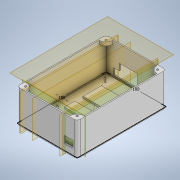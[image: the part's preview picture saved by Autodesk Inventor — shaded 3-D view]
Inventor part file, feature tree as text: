
AUTODESK INVENTOR PART (.ipt)
format: ipt  version: 2021 (Build 250183000, 183)  size: 476,160 bytes
history: native  units: in
note: dims shown in document units (in); Inventor stores cm internally (conversion verified against a paired STEP export)
features: sketch x25, extrude x19, reference x16, plane x7, mirror x4, other x4, revolve x2, chamfer x1, fillet x1
ambient origin geometry x8: Origin, YZ Plane, XZ Plane, XY Plane, X Axis, Y Axis, Z Axis, Center Point
bodies: Solid1 (feature_tree)
feature tree (79):
  sketch  "Sketch1"  dims[d0=3.937in d1=5.9055in]
  extrude  "Extrusion1"  Depth=5.9055in
  extrude  "Extrusion2"  Depth=2.1654in TaperAngle=0.0deg
  sketch  "Sketch2"  dims[d5=0.0787in d6=0.0in d7=-1.5748in]
  plane  "Work Plane1"
  extrude  "Extrusion3"  [1 undecoded]
  sketch  "Sketch7"  dims[d19=0.1181in d20=0.0in d21=2.8346in]
  plane  "Work Plane2"
  revolve  "Revolution2"  [1 undecoded]
  plane  "Work Plane3"
  extrude  "Extrusion4"  Depth=0.7087in
  sketch  "Sketch Driven Pattern1"  dims[d2=0.0787in d3=2.1654in d4=0.0in]
  extrude  "Extrusion5"  Depth=2.8346in
  plane  "Work Plane4"
  extrude  "Extrusion6"  Depth=0.1102in
  extrude  "Extrusion7"  Depth=0.1339in
  extrude  "Extrusion8"  TaperAngle=90.0deg  [1 undecoded]
  mirror  "Mirror1"
  plane  "Work Plane5"
  extrude  "Extrusion9"  Depth=0.0118in
  extrude  "Extrusion10"  Depth=0.0299in
  extrude  "Extrusion11"  Depth=0.0787in
  chamfer  "Chamfer1"  Distance=0.0787in
  extrude  "Extrusion12"  Depth=0.9055in
  sketch  "Sketch22"  dims[d47=0.5933in d48=0.0in d49=0.0866in]
  plane  "Work Plane6"
  revolve  "Revolution3"  [1 undecoded]
  extrude  "Extrusion13"  Depth=0.3819in
  sketch  "Sketch Driven Pattern2"  dims[d15=1.378in d16=1.2598in]
  extrude  "Extrusion14"  Depth=0.5933in
  extrude  "Extrusion15"  Depth=0.3236in
  extrude  "Extrusion16"  Depth=0.4724in
  plane  "Work Plane7"
  mirror  "Mirror2"
  extrude  "Extrusion17"  Depth=0.0787in TaperAngle=45.0deg
  extrude  "Extrusion18"  Depth=0.3937in
  extrude  "Extrusion19"  Depth=0.5933in
  mirror  "Mirror3"
  mirror  "Mirror4"
  fillet  "Fillet1"  Radius=0.5933in
  sketch  "Sketch6"  dims[d17=1.0236in d18=0.7087in]
  reference  "Reference1"
  reference  "Reference2"
  reference  "Reference3"
  reference  "Reference4"
  sketch  "Sketch8"  dims[d22=0.7087in d23=0.1102in]
  sketch  "Sketch9"  dims[d26=0.1063in d27=0.1339in]
  sketch  "Sketch10"  dims[d28=0.1929in d30=90.0deg]
  reference  "Reference5"
  reference  "Reference6"
  reference  "Reference7"
  reference  "Reference8"
  reference  "Reference9"
  reference  "Reference10"
  sketch  "Sketch11"  dims[d31=3.0in d32=0.0118in]
  sketch  "Sketch13"  dims[d33=0.1946in d34=0.0299in]
  sketch  "Sketch15"  dims[d35=0.0787in d36=0.0in d37=0.0157in]
  sketch  "Sketch18"  dims[d38=0.0157in d39=0.0787in d40=0.0in]
  sketch  "Sketch19"  dims[d41=0.9055in d42=1.1811in]
  sketch  "Sketch20"  dims[d43=0.4606in d44=0.9843in]
  sketch  "Sketch21"  dims[d45=0.0906in d46=0.3819in]
  reference  "Reference11"
  reference  "Reference12"
  reference  "Reference13"
  reference  "Reference14"
  reference  "Reference15"
  reference  "Reference16"
  sketch  "Sketch25"  dims[d50=0.4409in d51=0.3236in]
  sketch  "Sketch26"  dims[d52=0.5933in d53=0.0in d54=0.4724in]
  sketch  "Sketch27"  dims[d55=0.5933in d56=0.0in d57=0.1575in d58=0.0787in d59=45.0deg]
  sketch  "Sketch29"  dims[d63=0.3937in d64=0.0906in]
  sketch  "Sketch30"  dims[d65=0.4606in d66=0.9843in d67=0.5933in d68=0.0in]
  sketch  "Sketch31"  dims[d69=0.0866in]
  sketch  "Sketch34"  dims[d70=0.4409in]
  sketch  "Sketch35"  dims[d71=0.3236in d72=0.5933in d73=0.0in d74=0.4724in d75=0.5933in d76=0.0in d77=0.2756in d78=0.5906in d79=0.1181in d80=0.0in d81=90.0deg d82=0.0276in d83=0.0394in d84=0.0in d85=0.2362in d86=0.5906in d87=0.3937in d88=0.2697in d89=0.0in d90=0.1496in d91=0.0591in d92=0.0in d93=0.0906in d94=0.1969in d95=0.0in d96=0.689in d98=0.4724in d99=0.2362in d100=0.0in d101=0.2362in d102=0.2165in d103=0.2165in d104=0.0984in d105=0.0in d106=0.1299in d107=0.0in d108=0.0in d109=0.1969in]
  other  "Chestbox_with_electronical_devices.iam"
  other  "ArduinoMega_STEP_AP203:1"
  other  "TCA9548A Adfruit with Header:1"
  other  "Part57"
note: 4 required parameter values undecoded (feature->parameter linkage not recoverable at this tier; creation-order binding heuristic only, values carry confidence <= 0.55)